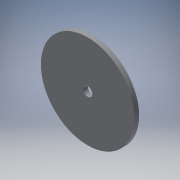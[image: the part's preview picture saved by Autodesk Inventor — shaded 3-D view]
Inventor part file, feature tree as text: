
AUTODESK INVENTOR PART (.ipt)
format: ipt  version: 2016 (Build 200138000, 138)  size: 94,208 bytes
history: native  units: in
note: dims shown in document units (in); Inventor stores cm internally (conversion verified against a paired STEP export)
features: extrude x2, sketch x2, reference x1
ambient origin geometry x8: Origin, YZ Plane, XZ Plane, XY Plane, X Axis, Y Axis, Z Axis, Center Point
bodies: Solid1 (feature_tree)
feature tree (5):
  extrude  "Extrusion1"  Depth=0.0394in TaperAngle=0.0deg
  extrude  "Extrusion2"  Depth=1.0in TaperAngle=0.0deg
  sketch  "Sketch1"  dims[d0=0.7874in d1=0.0394in d2=0.0in]
  reference  "Reference1"
  sketch  "Sketch2"  dims[d3=0.0787in d4=1.0in d5=0.0in]
